# Revit family: CADS_Vent-Axia_MechEquip_Fan_VSC_SabreSickleShortCased_3Ph6P - EXTRACT
name_source: partatom
category: Mechanical Equipment
units: mm (PartAtom-declared; Revit-internal decimal feet)

## family parameters
Always vertical = Yes
Cut with Voids When Loaded = No
OmniClass Number = 23.75.00.00
OmniClass Title = Climate Control (HVAC)
Part Type = Normal
Room Calculation Point = No
Round Connector Dimension = Use Diameter
Shared = No
Work Plane-Based = No

## types (5) — shared parameters
AirflowRateRange = 0.0 L/s
AssemblyPlace = UNKNOWN
AssetType = FIXED
DurationUnit = Year
ExteriorInsulation = No
Fitting Type = Ignore
GrossWeight = 0.00 kg
HasProtectiveEarth = No
IfcExportAs = IfcFanType
IsExtendedWarranty = No
ManufacturerAddress = Fleming Way
Crawley 
RH10 9YX
Quantity = 1
RatedCurrent = 0 A
RatedVoltage = 0 V
Status = New
WarrantyGuarantor = Vent-Axia Limited
WorkingPressure = 0.0 Pa
zero-valued in all types: CADS_Index, CADS_Usage, Default Elevation, ExpectedServiceLife, NumberOfPoles

## per-type parameters (varying)
| type | ModelReference | NominalDiameter | NominalHeight | NominalLength | NominalWidth |
| VSC45036 | SHORT CASE SICKLE FAN 450DIA 3PH 6 POLE | 450 mm  [stored 1.47638 ft] | 450 mm  [stored 1.47638 ft] | 160 mm  [stored 0.524934 ft] | 450 mm  [stored 1.47638 ft] |
| VSC50036 | SHORT CASE SICKLE FAN 500DIA 3PH 6 POLE | 500 mm  [stored 1.64042 ft] | 500 mm  [stored 1.64042 ft] | 166 mm  [stored 0.544619 ft] | 500 mm  [stored 1.64042 ft] |
| VSC56036 | SHORT CASE SICKLE FAN 560DIA 3PH 6 POLE | 560 mm  [stored 1.83727 ft] | 560 mm  [stored 1.83727 ft] | 210 mm  [stored 0.688976 ft] | 560 mm  [stored 1.83727 ft] |
| VSC63036B | 630MM 3PH 6P CASED FAN | 630 mm  [stored 2.06693 ft] | 630 mm  [stored 2.06693 ft] | 226 mm | 630 mm  [stored 2.06693 ft] |
| VSC71036A | OWLET SICKLE CASE FAN 710DIA 3PH 6 POLE | 710 mm | 710 mm | 260 mm  [stored 0.853018 ft] | 710 mm |

note: column(s) folded — value = type name in every type: ModelNumber

note: [stored X ft] marks values corroborated as IEEE doubles in the binary element streams (Revit-internal decimal feet)

## geometry (parser evidence)
native form markers: Sweep x9
no freeform markers — native parametric forms only
